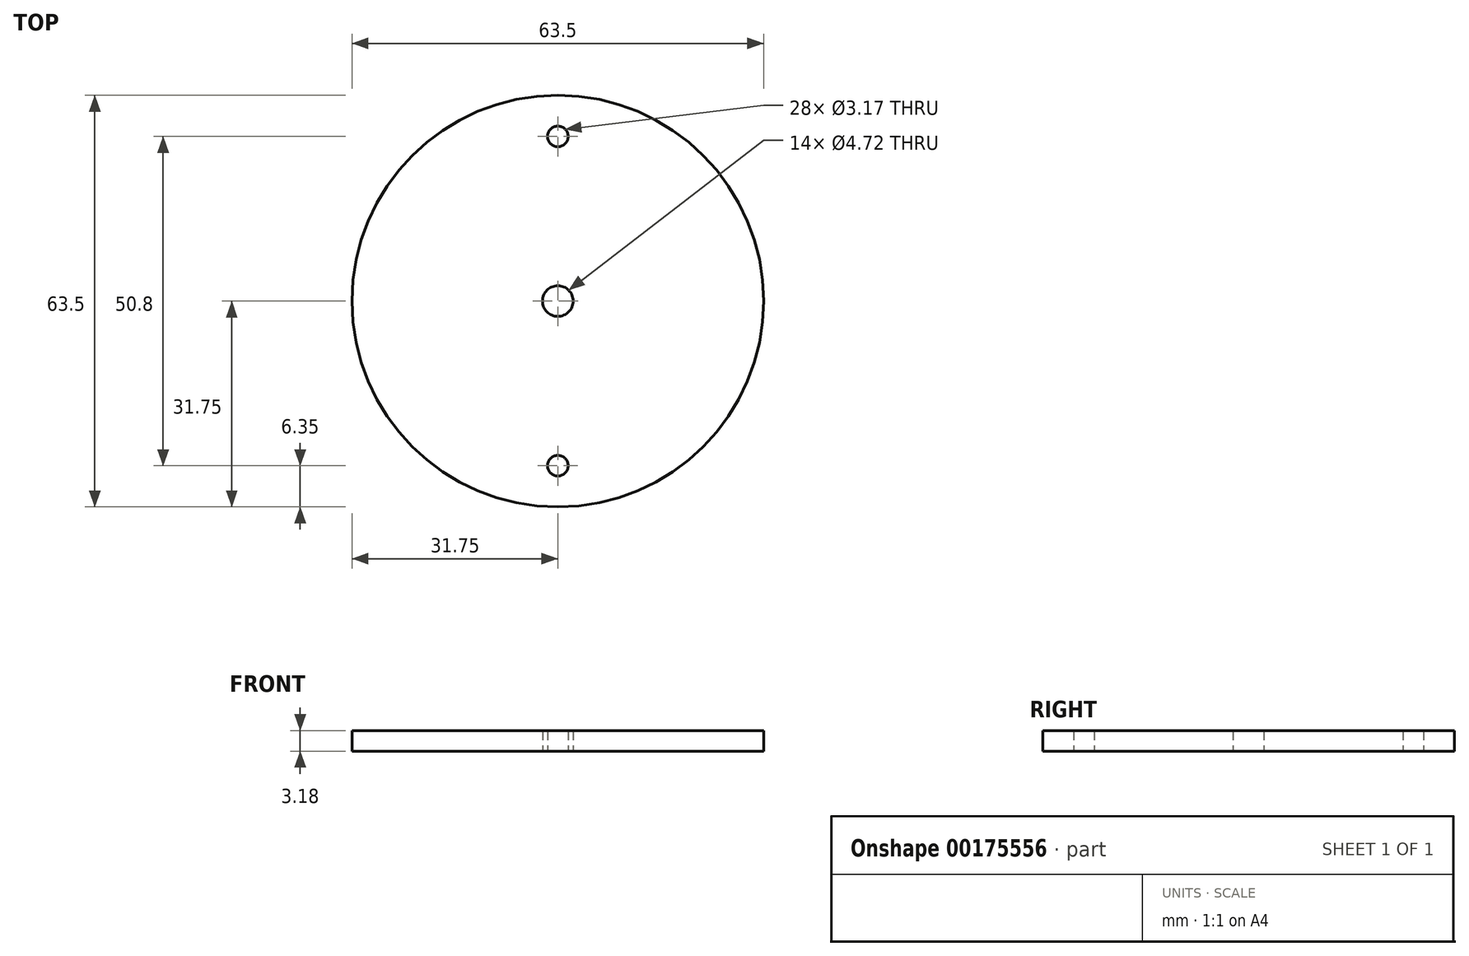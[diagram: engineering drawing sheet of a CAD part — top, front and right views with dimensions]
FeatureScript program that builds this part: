
annotation { "Feature Type Name" : "Feature", "Feature Type Description" : "" }
export const myFeature = defineFeature(function(context is Context, id is Id, definition is map)
    precondition{}
    {
        {
            var Q0;
            Q0=qCreatedBy(makeId("Top.planeOp"),FACE);
            var sketch = newSketch(context, id + "F0", { "sketchPlane" : qUnion([Q0])});
            skCircle(sketch, "E0", {"center": v(0, 0) * mm, "radius": 31.75 * mm});
            skCircle(sketch, "E1", {"center": v(0, 25.4) * mm, "radius": 1.59 * mm});
            skLineSegment(sketch, "E2", {"start": v(-31.75, 0) * mm, "end": v(31.75, 0) * mm, "construction": true});
            skCircle(sketch, "E3.MirrorC", {"center": v(0, -25.4) * mm, "radius": 1.59 * mm});
            skCircle(sketch, "E4", {"center": v(0, 0) * mm, "radius": 2.36 * mm});
            skSolve(sketch);
        }
        {
            var Q0;
            Q0 = qSketchRegion(id + "F0", true);
            extrude(context, id + "F1", {"entities" : qUnion([Q0]), "depth" : 3.17 * mm});
        }
    });
